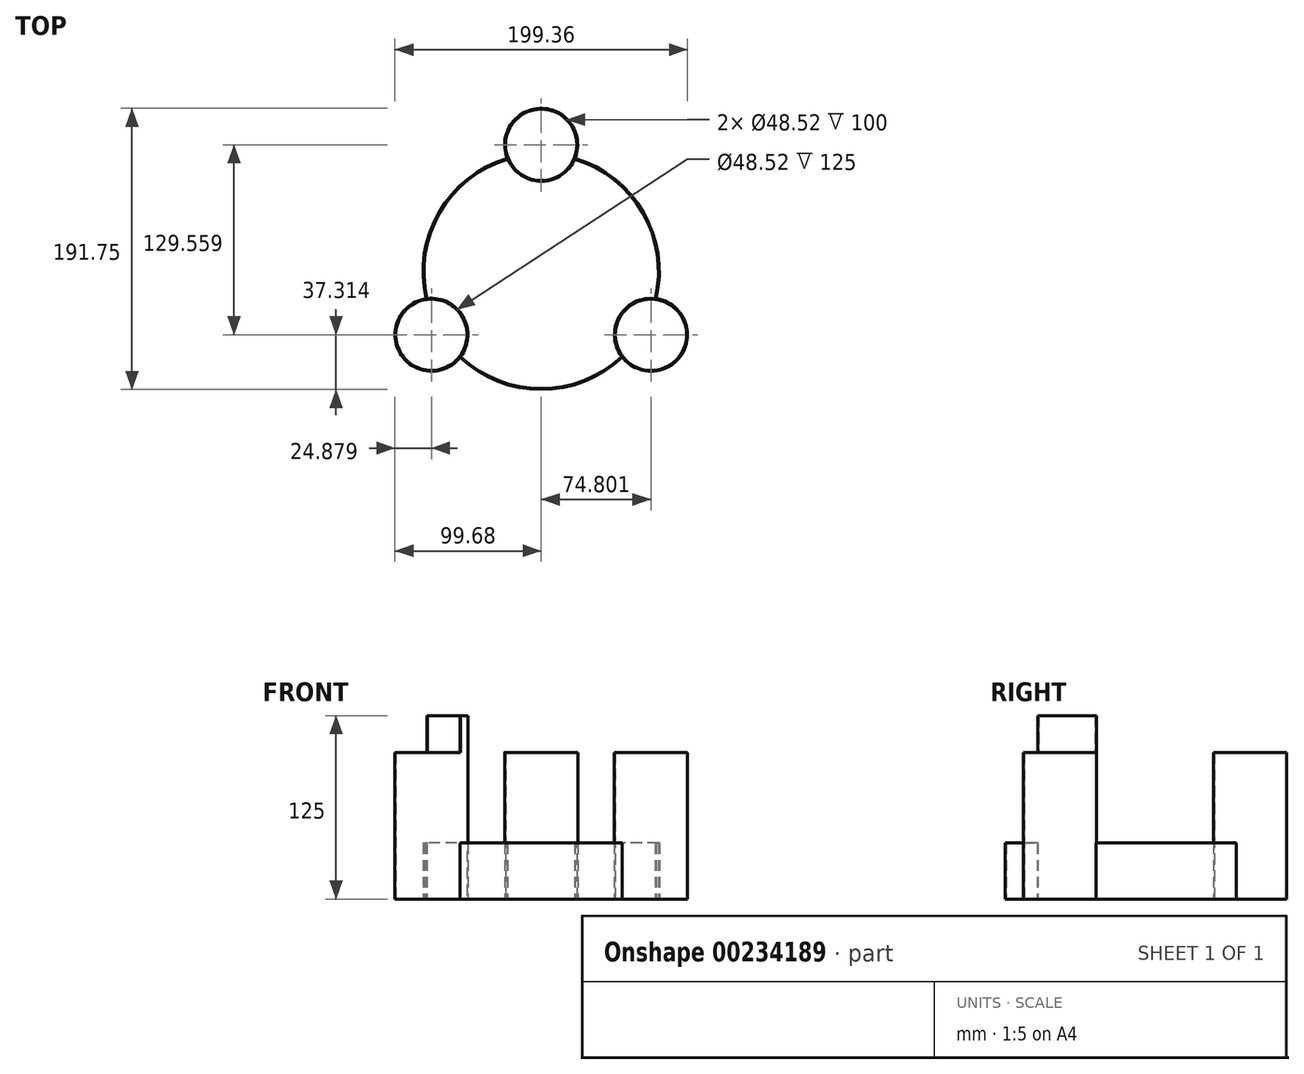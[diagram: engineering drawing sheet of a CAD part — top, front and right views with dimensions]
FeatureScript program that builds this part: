
annotation { "Feature Type Name" : "Feature", "Feature Type Description" : "" }
export const myFeature = defineFeature(function(context is Context, id is Id, definition is map)
    precondition{}
    {
        {
            assignVariable(context, id + "F0", {"name" : "or", "anyValue" : 1 / 1.62});
        }
        {
            assignVariable(context, id + "F1", {"name" : "height", "anyValue" : 100});
        }
        {
            assignVariable(context, id + "F2", {"name" : "armheight", "anyValue" : getVariable(context, 'height') * getVariable(context, 'or')});
        }
        {
            assignVariable(context, id + "F3", {"name" : "elementheight", "anyValue" : getVariable(context, 'height') - getVariable(context, 'armheight')});
        }
        {
            var Q0;
            Q0=qCreatedBy(makeId("Top.planeOp"),FACE);
            var sketch = newSketch(context, id + "F4", { "sketchPlane" : qUnion([Q0])});
            skCircle(sketch, "E0", {"center": v(0, 0) * mm, "radius": 80.5 * mm});
            skCircle(sketch, "E1", {"center": v(0, 0) * mm, "radius": 79.88 * mm});
            skCircle(sketch, "E2", {"center": v(0, 86.37) * mm, "radius": 24.88 * mm});
            skLineSegment(sketch, "E3", {"start": v(0, 86.37) * mm, "end": v(0, 0) * mm, "construction": true});
            skCircle(sketch, "E4.1.0", {"center": v(-74.8, -43.19) * mm, "radius": 24.88 * mm});
            skCircle(sketch, "E4.2.0", {"center": v(74.8, -43.19) * mm, "radius": 24.88 * mm});
            skLineSegment(sketch, "E5", {"start": v(-74.8, -43.19) * mm, "end": v(0, 0) * mm, "construction": true});
            skLineSegment(sketch, "E6", {"start": v(0, 0) * mm, "end": v(74.8, -43.19) * mm, "construction": true});
            skCircle(sketch, "E7", {"center": v(74.8, -43.19) * mm, "radius": 24.26 * mm});
            skCircle(sketch, "E8", {"center": v(-74.8, -43.19) * mm, "radius": 24.26 * mm});
            skCircle(sketch, "E9", {"center": v(0, 86.37) * mm, "radius": 24.26 * mm});
            skSolve(sketch);
        }
        {
            var Q0;
            {var subQ0=sQuery(id+"F4.wireOp",EDGE,"E4.2.0");var subQ1=sQuery(id+"F4.wireOp",EDGE,"E0");var subQ2=makeQuery(id+"F4.imprint","INTERSECT",VERTEX,{"disambiguationData":[OD(0.0)],"derivedFrom":[subQ1,subQ0]});Q0=makeQuery(id+"F4.imprint","IMPRINT",FACE,{"disambiguationData":[TD([[makeQuery(id+"F4.imprint","IMPRINT",EDGE,{"disambiguationData":[TD([[subQ2,-1.0]])],"derivedFrom":subQ1}),1.0]])]});}
            var Q1;
            {var subQ0=sQuery(id+"F4.wireOp",EDGE,"E4.1.0");var subQ1=sQuery(id+"F4.wireOp",EDGE,"E0");var subQ2=makeQuery(id+"F4.imprint","INTERSECT",VERTEX,{"disambiguationData":[OD(1.0)],"derivedFrom":[subQ1,subQ0]});Q1=makeQuery(id+"F4.imprint","IMPRINT",FACE,{"disambiguationData":[TD([[makeQuery(id+"F4.imprint","IMPRINT",EDGE,{"disambiguationData":[TD([[subQ2,-1.0]])],"derivedFrom":subQ1}),1.0]])]});}
            var Q2;
            {var subQ0=sQuery(id+"F4.wireOp",EDGE,"E4.1.0");var subQ1=sQuery(id+"F4.wireOp",EDGE,"E0");var subQ2=makeQuery(id+"F4.imprint","INTERSECT",VERTEX,{"disambiguationData":[OD(1.0)],"derivedFrom":[subQ1,subQ0]});Q2=makeQuery(id+"F4.imprint","IMPRINT",FACE,{"disambiguationData":[TD([[makeQuery(id+"F4.imprint","IMPRINT",EDGE,{"disambiguationData":[TD([[subQ2,1.0]])],"derivedFrom":subQ1}),1.0]])]});}
            var Q3;
            {var subQ0=sQuery(id+"F4.wireOp",EDGE,"E2");var subQ1=sQuery(id+"F4.wireOp",EDGE,"E0");var subQ2=makeQuery(id+"F4.imprint","INTERSECT",VERTEX,{"disambiguationData":[OD(1.0)],"derivedFrom":[subQ1,subQ0]});Q3=makeQuery(id+"F4.imprint","IMPRINT",FACE,{"disambiguationData":[TD([[makeQuery(id+"F4.imprint","IMPRINT",EDGE,{"disambiguationData":[TD([[subQ2,-1.0]])],"derivedFrom":subQ1}),1.0]])]});}
            var Q4;
            {var subQ0=sQuery(id+"F4.wireOp",EDGE,"E4.1.0");var subQ1=sQuery(id+"F4.wireOp",EDGE,"E0");var subQ2=makeQuery(id+"F4.imprint","INTERSECT",VERTEX,{"disambiguationData":[OD(0.0)],"derivedFrom":[subQ1,subQ0]});Q4=makeQuery(id+"F4.imprint","IMPRINT",FACE,{"disambiguationData":[TD([[makeQuery(id+"F4.imprint","IMPRINT",EDGE,{"disambiguationData":[TD([[subQ2,-1.0]])],"derivedFrom":subQ1}),1.0]])]});}
            var Q5;
            {var subQ0=sQuery(id+"F4.wireOp",EDGE,"E2");var subQ1=sQuery(id+"F4.wireOp",EDGE,"E0");var subQ2=makeQuery(id+"F4.imprint","INTERSECT",VERTEX,{"disambiguationData":[OD(1.0)],"derivedFrom":[subQ1,subQ0]});Q5=makeQuery(id+"F4.imprint","IMPRINT",FACE,{"disambiguationData":[TD([[makeQuery(id+"F4.imprint","IMPRINT",EDGE,{"disambiguationData":[TD([[subQ2,1.0]])],"derivedFrom":subQ1}),1.0]])]});}
            var Q6;
            {var subQ0=sQuery(id+"F4.wireOp",EDGE,"E2");var subQ1=sQuery(id+"F4.wireOp",EDGE,"E0");var subQ2=makeQuery(id+"F4.imprint","INTERSECT",VERTEX,{"disambiguationData":[OD(0.0)],"derivedFrom":[subQ1,subQ0]});Q6=makeQuery(id+"F4.imprint","IMPRINT",FACE,{"disambiguationData":[TD([[makeQuery(id+"F4.imprint","IMPRINT",EDGE,{"disambiguationData":[TD([[subQ2,-1.0]])],"derivedFrom":subQ1}),1.0]])]});}
            var Q7;
            {var subQ0=sQuery(id+"F4.wireOp",EDGE,"E2");var subQ1=sQuery(id+"F4.wireOp",EDGE,"E0");var subQ2=makeQuery(id+"F4.imprint","INTERSECT",VERTEX,{"disambiguationData":[OD(0.0)],"derivedFrom":[subQ1,subQ0]});Q7=makeQuery(id+"F4.imprint","IMPRINT",FACE,{"disambiguationData":[TD([[makeQuery(id+"F4.imprint","IMPRINT",EDGE,{"disambiguationData":[TD([[subQ2,1.0]])],"derivedFrom":subQ1}),1.0]])]});}
            var Q8;
            {var subQ0=sQuery(id+"F4.wireOp",EDGE,"E4.2.0");var subQ1=sQuery(id+"F4.wireOp",EDGE,"E0");var subQ2=makeQuery(id+"F4.imprint","INTERSECT",VERTEX,{"disambiguationData":[OD(1.0)],"derivedFrom":[subQ1,subQ0]});Q8=makeQuery(id+"F4.imprint","IMPRINT",FACE,{"disambiguationData":[TD([[makeQuery(id+"F4.imprint","IMPRINT",EDGE,{"disambiguationData":[TD([[subQ2,1.0]])],"derivedFrom":subQ1}),1.0]])]});}
            var Q9;
            {var subQ0=sQuery(id+"F4.wireOp",EDGE,"E4.2.0");var subQ1=sQuery(id+"F4.wireOp",EDGE,"E0");var subQ2=makeQuery(id+"F4.imprint","INTERSECT",VERTEX,{"disambiguationData":[OD(0.0)],"derivedFrom":[subQ1,subQ0]});Q9=makeQuery(id+"F4.imprint","IMPRINT",FACE,{"disambiguationData":[TD([[makeQuery(id+"F4.imprint","IMPRINT",EDGE,{"disambiguationData":[TD([[subQ2,-1.0]])],"derivedFrom":subQ1}),-1.0]])]});}
            var Q10;
            {var subQ0=sQuery(id+"F4.wireOp",EDGE,"E4.2.0");var subQ1=sQuery(id+"F4.wireOp",EDGE,"E1");var subQ2=makeQuery(id+"F4.imprint","INTERSECT",VERTEX,{"disambiguationData":[OD(0.0)],"derivedFrom":[subQ1,subQ0]});Q10=makeQuery(id+"F4.imprint","IMPRINT",FACE,{"disambiguationData":[TD([[makeQuery(id+"F4.imprint","IMPRINT",EDGE,{"disambiguationData":[TD([[subQ2,-1.0]])],"derivedFrom":subQ1}),1.0]])]});}
            var Q11;
            {var subQ0=sQuery(id+"F4.wireOp",EDGE,"E9");var subQ1=sQuery(id+"F4.wireOp",EDGE,"E1");var subQ2=makeQuery(id+"F4.imprint","INTERSECT",VERTEX,{"disambiguationData":[OD(0.0)],"derivedFrom":[subQ1,subQ0]});Q11=makeQuery(id+"F4.imprint","IMPRINT",FACE,{"disambiguationData":[TD([[makeQuery(id+"F4.imprint","IMPRINT",EDGE,{"disambiguationData":[TD([[subQ2,1.0]])],"derivedFrom":subQ1}),1.0]])]});}
            var Q12;
            {var subQ0=sQuery(id+"F4.wireOp",EDGE,"E2");var subQ1=sQuery(id+"F4.wireOp",EDGE,"E0");var subQ2=makeQuery(id+"F4.imprint","INTERSECT",VERTEX,{"disambiguationData":[OD(0.0)],"derivedFrom":[subQ1,subQ0]});Q12=makeQuery(id+"F4.imprint","IMPRINT",FACE,{"disambiguationData":[TD([[makeQuery(id+"F4.imprint","IMPRINT",EDGE,{"disambiguationData":[TD([[subQ2,-1.0]])],"derivedFrom":subQ1}),-1.0]])]});}
            var Q13;
            {var subQ0=sQuery(id+"F4.wireOp",EDGE,"E4.1.0");var subQ1=sQuery(id+"F4.wireOp",EDGE,"E0");var subQ2=makeQuery(id+"F4.imprint","INTERSECT",VERTEX,{"disambiguationData":[OD(0.0)],"derivedFrom":[subQ1,subQ0]});Q13=makeQuery(id+"F4.imprint","IMPRINT",FACE,{"disambiguationData":[TD([[makeQuery(id+"F4.imprint","IMPRINT",EDGE,{"disambiguationData":[TD([[subQ2,-1.0]])],"derivedFrom":subQ1}),-1.0]])]});}
            var Q14;
            {var subQ0=sQuery(id+"F4.wireOp",EDGE,"E4.1.0");var subQ1=sQuery(id+"F4.wireOp",EDGE,"E1");var subQ2=makeQuery(id+"F4.imprint","INTERSECT",VERTEX,{"disambiguationData":[OD(0.0)],"derivedFrom":[subQ1,subQ0]});Q14=makeQuery(id+"F4.imprint","IMPRINT",FACE,{"disambiguationData":[TD([[makeQuery(id+"F4.imprint","IMPRINT",EDGE,{"disambiguationData":[TD([[subQ2,-1.0]])],"derivedFrom":subQ1}),1.0]])]});}
            extrude(context, id + "F5", {"entities" : qUnion([Q0, Q1, Q2, Q3, Q4, Q5, Q6, Q7, Q8, Q9, Q10, Q11, Q12, Q13, Q14]), "depth" : (getVariable(context, 'elementheight')) * mm});
        }
        {
            var Q0;
            {var subQ0=sQuery(id+"F4.wireOp",EDGE,"E4.1.0");var subQ1=sQuery(id+"F4.wireOp",EDGE,"E1");var subQ2=makeQuery(id+"F4.imprint","INTERSECT",VERTEX,{"disambiguationData":[OD(0.0)],"derivedFrom":[subQ1,subQ0]});Q0=makeQuery(id+"F4.imprint","IMPRINT",FACE,{"disambiguationData":[TD([[makeQuery(id+"F4.imprint","IMPRINT",EDGE,{"disambiguationData":[TD([[subQ2,-1.0]])],"derivedFrom":subQ1}),1.0]])]});}
            var Q1;
            {var subQ0=sQuery(id+"F4.wireOp",EDGE,"E4.2.0");var subQ1=sQuery(id+"F4.wireOp",EDGE,"E1");var subQ2=makeQuery(id+"F4.imprint","INTERSECT",VERTEX,{"disambiguationData":[OD(0.0)],"derivedFrom":[subQ1,subQ0]});Q1=makeQuery(id+"F4.imprint","IMPRINT",FACE,{"disambiguationData":[TD([[makeQuery(id+"F4.imprint","IMPRINT",EDGE,{"disambiguationData":[TD([[subQ2,-1.0]])],"derivedFrom":subQ1}),1.0]])]});}
            var Q2;
            {var subQ0=sQuery(id+"F4.wireOp",EDGE,"E4.2.0");var subQ1=sQuery(id+"F4.wireOp",EDGE,"E0");var subQ2=makeQuery(id+"F4.imprint","INTERSECT",VERTEX,{"disambiguationData":[OD(0.0)],"derivedFrom":[subQ1,subQ0]});Q2=makeQuery(id+"F4.imprint","IMPRINT",FACE,{"disambiguationData":[TD([[makeQuery(id+"F4.imprint","IMPRINT",EDGE,{"disambiguationData":[TD([[subQ2,-1.0]])],"derivedFrom":subQ1}),1.0]])]});}
            var Q3;
            {var subQ0=sQuery(id+"F4.wireOp",EDGE,"E4.2.0");var subQ1=sQuery(id+"F4.wireOp",EDGE,"E0");var subQ2=makeQuery(id+"F4.imprint","INTERSECT",VERTEX,{"disambiguationData":[OD(1.0)],"derivedFrom":[subQ1,subQ0]});Q3=makeQuery(id+"F4.imprint","IMPRINT",FACE,{"disambiguationData":[TD([[makeQuery(id+"F4.imprint","IMPRINT",EDGE,{"disambiguationData":[TD([[subQ2,1.0]])],"derivedFrom":subQ1}),1.0]])]});}
            var Q4;
            {var subQ0=sQuery(id+"F4.wireOp",EDGE,"E4.1.0");var subQ1=sQuery(id+"F4.wireOp",EDGE,"E0");var subQ2=makeQuery(id+"F4.imprint","INTERSECT",VERTEX,{"disambiguationData":[OD(0.0)],"derivedFrom":[subQ1,subQ0]});Q4=makeQuery(id+"F4.imprint","IMPRINT",FACE,{"disambiguationData":[TD([[makeQuery(id+"F4.imprint","IMPRINT",EDGE,{"disambiguationData":[TD([[subQ2,-1.0]])],"derivedFrom":subQ1}),1.0]])]});}
            var Q5;
            {var subQ0=sQuery(id+"F4.wireOp",EDGE,"E4.1.0");var subQ1=sQuery(id+"F4.wireOp",EDGE,"E0");var subQ2=makeQuery(id+"F4.imprint","INTERSECT",VERTEX,{"disambiguationData":[OD(1.0)],"derivedFrom":[subQ1,subQ0]});Q5=makeQuery(id+"F4.imprint","IMPRINT",FACE,{"disambiguationData":[TD([[makeQuery(id+"F4.imprint","IMPRINT",EDGE,{"disambiguationData":[TD([[subQ2,1.0]])],"derivedFrom":subQ1}),1.0]])]});}
            var Q6;
            {var subQ0=sQuery(id+"F4.wireOp",EDGE,"E2");var subQ1=sQuery(id+"F4.wireOp",EDGE,"E0");var subQ2=makeQuery(id+"F4.imprint","INTERSECT",VERTEX,{"disambiguationData":[OD(1.0)],"derivedFrom":[subQ1,subQ0]});Q6=makeQuery(id+"F4.imprint","IMPRINT",FACE,{"disambiguationData":[TD([[makeQuery(id+"F4.imprint","IMPRINT",EDGE,{"disambiguationData":[TD([[subQ2,1.0]])],"derivedFrom":subQ1}),1.0]])]});}
            var Q7;
            {var subQ0=sQuery(id+"F4.wireOp",EDGE,"E9");var subQ1=sQuery(id+"F4.wireOp",EDGE,"E1");var subQ2=makeQuery(id+"F4.imprint","INTERSECT",VERTEX,{"disambiguationData":[OD(0.0)],"derivedFrom":[subQ1,subQ0]});Q7=makeQuery(id+"F4.imprint","IMPRINT",FACE,{"disambiguationData":[TD([[makeQuery(id+"F4.imprint","IMPRINT",EDGE,{"disambiguationData":[TD([[subQ2,1.0]])],"derivedFrom":subQ1}),1.0]])]});}
            var Q8;
            {var subQ0=sQuery(id+"F4.wireOp",EDGE,"E2");var subQ1=sQuery(id+"F4.wireOp",EDGE,"E0");var subQ2=makeQuery(id+"F4.imprint","INTERSECT",VERTEX,{"disambiguationData":[OD(0.0)],"derivedFrom":[subQ1,subQ0]});Q8=makeQuery(id+"F4.imprint","IMPRINT",FACE,{"disambiguationData":[TD([[makeQuery(id+"F4.imprint","IMPRINT",EDGE,{"disambiguationData":[TD([[subQ2,-1.0]])],"derivedFrom":subQ1}),1.0]])]});}
            var Q9;
            {var subQ0=sQuery(id+"F4.wireOp",EDGE,"E2");var subQ1=sQuery(id+"F4.wireOp",EDGE,"E0");var subQ2=makeQuery(id+"F4.imprint","INTERSECT",VERTEX,{"disambiguationData":[OD(0.0)],"derivedFrom":[subQ1,subQ0]});Q9=makeQuery(id+"F4.imprint","IMPRINT",FACE,{"disambiguationData":[TD([[makeQuery(id+"F4.imprint","IMPRINT",EDGE,{"disambiguationData":[TD([[subQ2,-1.0]])],"derivedFrom":subQ1}),-1.0]])]});}
            var Q10;
            {var subQ0=sQuery(id+"F4.wireOp",EDGE,"E4.1.0");var subQ1=sQuery(id+"F4.wireOp",EDGE,"E0");var subQ2=makeQuery(id+"F4.imprint","INTERSECT",VERTEX,{"disambiguationData":[OD(0.0)],"derivedFrom":[subQ1,subQ0]});Q10=makeQuery(id+"F4.imprint","IMPRINT",FACE,{"disambiguationData":[TD([[makeQuery(id+"F4.imprint","IMPRINT",EDGE,{"disambiguationData":[TD([[subQ2,-1.0]])],"derivedFrom":subQ1}),-1.0]])]});}
            var Q11;
            {var subQ0=sQuery(id+"F4.wireOp",EDGE,"E4.2.0");var subQ1=sQuery(id+"F4.wireOp",EDGE,"E0");var subQ2=makeQuery(id+"F4.imprint","INTERSECT",VERTEX,{"disambiguationData":[OD(0.0)],"derivedFrom":[subQ1,subQ0]});Q11=makeQuery(id+"F4.imprint","IMPRINT",FACE,{"disambiguationData":[TD([[makeQuery(id+"F4.imprint","IMPRINT",EDGE,{"disambiguationData":[TD([[subQ2,-1.0]])],"derivedFrom":subQ1}),-1.0]])]});}
            extrude(context, id + "F6", {"entities" : qUnion([Q0, Q1, Q2, Q3, Q4, Q5, Q6, Q7, Q8, Q9, Q10, Q11]), "operationType" : NewBodyOperationType.ADD, "depth" : (getVariable(context, 'elementheight') + getVariable(context, 'armheight')) * mm});
        }
        {
            var Q0;
            Q0=makeQuery(id+"F6.opExtrude","CAP_FACE",FACE,{"disambiguationData":[OSD([sQuery(id+"F4.wireOp",EDGE,"E4.1.0")])],"isStart":false});
            var sketch = newSketch(context, id + "F7", { "sketchPlane" : qUnion([Q0])});
            skCircle(sketch, "E10.0", {"center": v(-74.8, -43.19) * mm, "radius": 24.88 * mm, "construction": true});
            skCircle(sketch, "E11.0", {"center": v(0, 86.37) * mm, "radius": 24.88 * mm, "construction": true});
            skCircle(sketch, "E12.0", {"center": v(74.8, -43.19) * mm, "radius": 24.88 * mm, "construction": true});
            skCircle(sketch, "E13.0", {"center": v(0, 0) * mm, "radius": 79.88 * mm, "construction": true});
            skArc(sketch, "E14", {"start": v(-77.71, -18.48) * mm, "mid": v(-69.18, -39.94) * mm, "end": v(-54.86, -58.06) * mm});
            skArc(sketch, "E15", {"start": v(-22.85, 76.54) * mm, "mid": v(0, 79.88) * mm, "end": v(22.85, 76.54) * mm});
            skArc(sketch, "E16", {"start": v(77.71, -18.48) * mm, "mid": v(69.18, -39.94) * mm, "end": v(54.86, -58.06) * mm});
            skArc(sketch, "E17", {"start": v(54.86, -58.06) * mm, "mid": v(53.26, -30.75) * mm, "end": v(77.71, -18.48) * mm});
            skArc(sketch, "E18", {"start": v(22.85, 76.54) * mm, "mid": v(0, 61.5) * mm, "end": v(-22.85, 76.54) * mm});
            skArc(sketch, "E19", {"start": v(-54.86, -58.06) * mm, "mid": v(-53.26, -30.75) * mm, "end": v(-77.71, -18.48) * mm});
            skCircle(sketch, "E20.0", {"center": v(74.8, -43.19) * mm, "radius": 24.26 * mm});
            skCircle(sketch, "E21.0", {"center": v(0, 86.37) * mm, "radius": 24.26 * mm});
            skCircle(sketch, "E22.0", {"center": v(-74.8, -43.19) * mm, "radius": 24.26 * mm});
            skSolve(sketch);
        }
        {
            var Q0;
            {var subQ0=sQuery(id+"F7.wireOp",EDGE,"E19");Q0=makeQuery(id+"F7.imprint","IMPRINT",FACE,{"disambiguationData":[TD([[makeQuery(id+"F7.imprint","IMPRINT",EDGE,{"derivedFrom":subQ0}),1.0]])]});}
            var Q1;
            {var subQ0=sQuery(id+"F7.wireOp",EDGE,"E18");Q1=makeQuery(id+"F7.imprint","IMPRINT",FACE,{"disambiguationData":[TD([[makeQuery(id+"F7.imprint","IMPRINT",EDGE,{"derivedFrom":subQ0}),-1.0]])]});}
            var Q2;
            {var subQ0=sQuery(id+"F7.wireOp",EDGE,"E17");Q2=makeQuery(id+"F7.imprint","IMPRINT",FACE,{"disambiguationData":[TD([[makeQuery(id+"F7.imprint","IMPRINT",EDGE,{"derivedFrom":subQ0}),-1.0]])]});}
            extrude(context, id + "F8", {"entities" : qUnion([Q0, Q1, Q2]), "operationType" : NewBodyOperationType.ADD, "depth" : 25 * mm});
        }
    });
